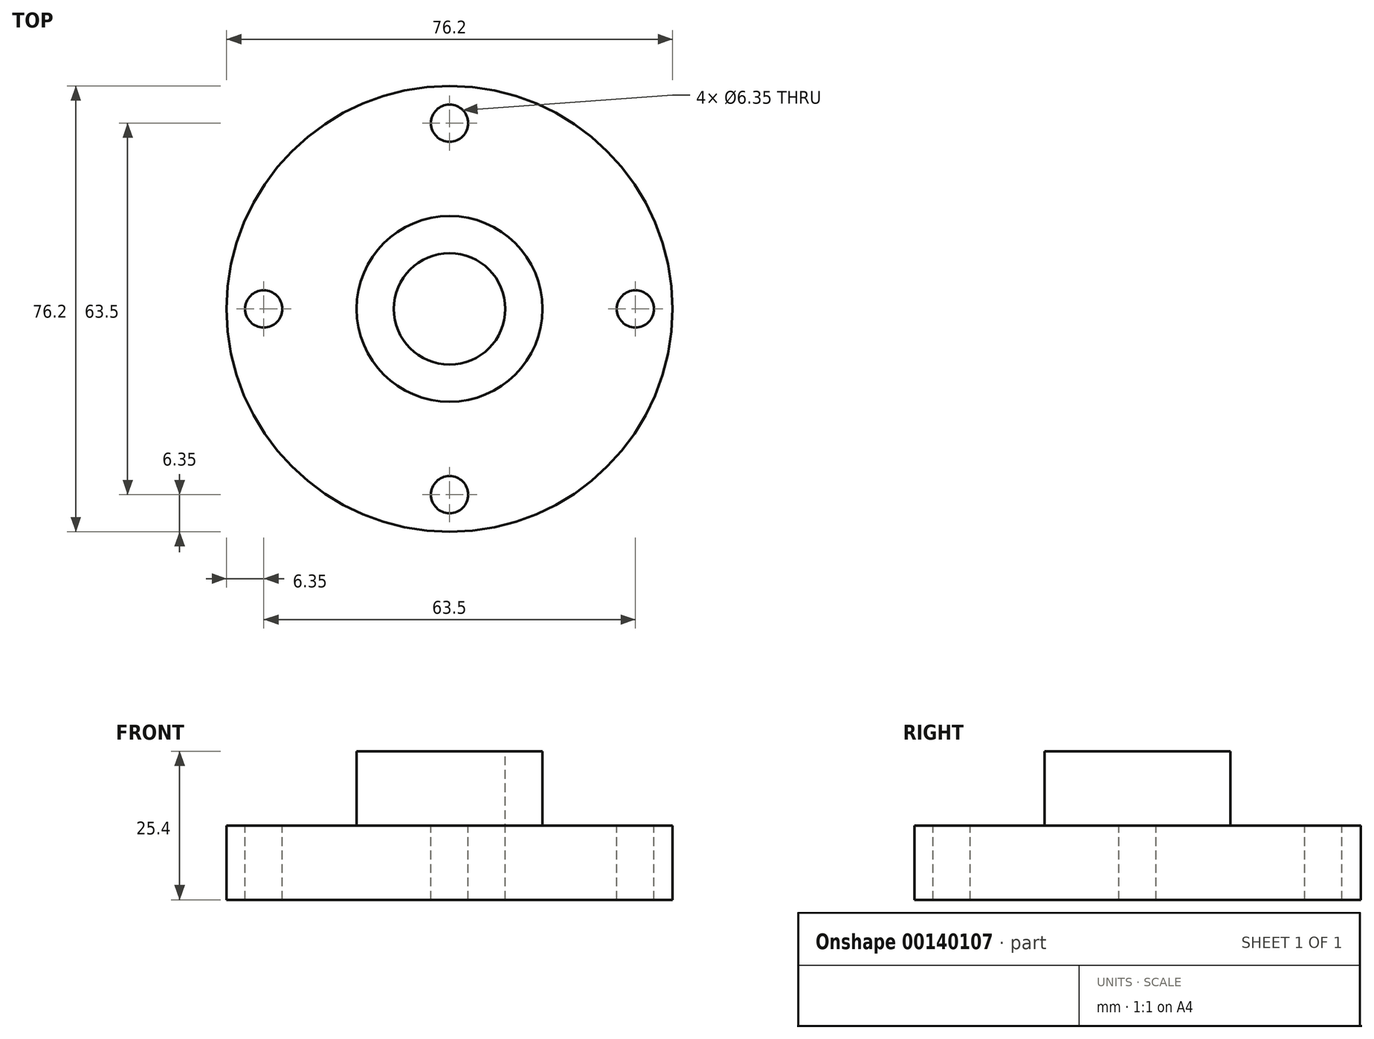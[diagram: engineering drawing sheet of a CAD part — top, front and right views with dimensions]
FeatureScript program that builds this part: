
annotation { "Feature Type Name" : "Feature", "Feature Type Description" : "" }
export const myFeature = defineFeature(function(context is Context, id is Id, definition is map)
    precondition{}
    {
        {
            var Q0;
            Q0=qCreatedBy(makeId("Front.planeOp"),FACE);
            var sketch = newSketch(context, id + "F0", { "sketchPlane" : qUnion([Q0])});
            skLineSegment(sketch, "E0", {"start": v(0, 0) * mm, "end": v(0, 25.4) * mm});
            skLineSegment(sketch, "E1", {"start": v(0, 25.4) * mm, "end": v(-15.88, 25.4) * mm});
            skLineSegment(sketch, "E2", {"start": v(-15.87, 25.4) * mm, "end": v(-15.87, 12.7) * mm});
            skLineSegment(sketch, "E3", {"start": v(-15.88, 12.7) * mm, "end": v(-38.1, 12.7) * mm});
            skLineSegment(sketch, "E4", {"start": v(-38.1, 12.7) * mm, "end": v(-38.1, 0) * mm});
            skLineSegment(sketch, "E5", {"start": v(-38.1, 0) * mm, "end": v(0, 0) * mm});
            skLineSegment(sketch, "E6", {"start": v(-15.88, 12.7) * mm, "end": v(0, 12.7) * mm});
            skLineSegment(sketch, "E7", {"start": v(0, 0) * mm, "end": v(0, 36.44) * mm, "construction": true});
            skSolve(sketch);
        }
        {
            var Q0;
            Q0 = qSketchRegion(id + "F0", true);
            var Q1;
            Q1=sQuery(id+"F0.wireOp",EDGE,"E7");
            revolve(context, id + "F1", {"entities" : qUnion([Q0]), "axis" : qUnion([Q1]), "revolveType" : RevolveType.FULL});
        }
        {
            var Q0;
            Q0=makeQuery(id+"F1.opRevolve","SWEPT_FACE",FACE,{"disambiguationData":[OSD([sQuery(id+"F0.wireOp",EDGE,"E3")])]});
            var sketch = newSketch(context, id + "F2", { "sketchPlane" : qUnion([Q0])});
            skCircle(sketch, "E8", {"center": v(0, 31.75) * mm, "radius": 3.18 * mm});
            skCircle(sketch, "E9.1.0", {"center": v(-31.75, 0) * mm, "radius": 3.18 * mm});
            skCircle(sketch, "E9.2.0", {"center": v(0, -31.75) * mm, "radius": 3.18 * mm});
            skCircle(sketch, "E9.3.0", {"center": v(31.75, 0) * mm, "radius": 3.18 * mm});
            skPoint(sketch, "E9.center", {"position": v(0, 0) * mm});
            skSolve(sketch);
        }
        {
            var Q0;
            Q0 = qSketchRegion(id + "F2", true);
            extrude(context, id + "F3", {"entities" : qUnion([Q0]), "operationType" : NewBodyOperationType.REMOVE, "oppositeDirection" : true, "depth" : 25.4 * mm});
        }
        {
            var Q0;
            Q0=makeQuery(id+"F1.opRevolve","SWEPT_FACE",FACE,{"disambiguationData":[OSD([sQuery(id+"F0.wireOp",EDGE,"E1")])]});
            var sketch = newSketch(context, id + "F4", { "sketchPlane" : qUnion([Q0])});
            skCircle(sketch, "E10", {"center": v(0, 0) * mm, "radius": 9.52 * mm});
            skSolve(sketch);
        }
        {
            var Q0;
            Q0 = qSketchRegion(id + "F4", true);
            extrude(context, id + "F5", {"entities" : qUnion([Q0]), "operationType" : NewBodyOperationType.REMOVE, "oppositeDirection" : true, "depth" : 50.52 * mm});
        }
    });
